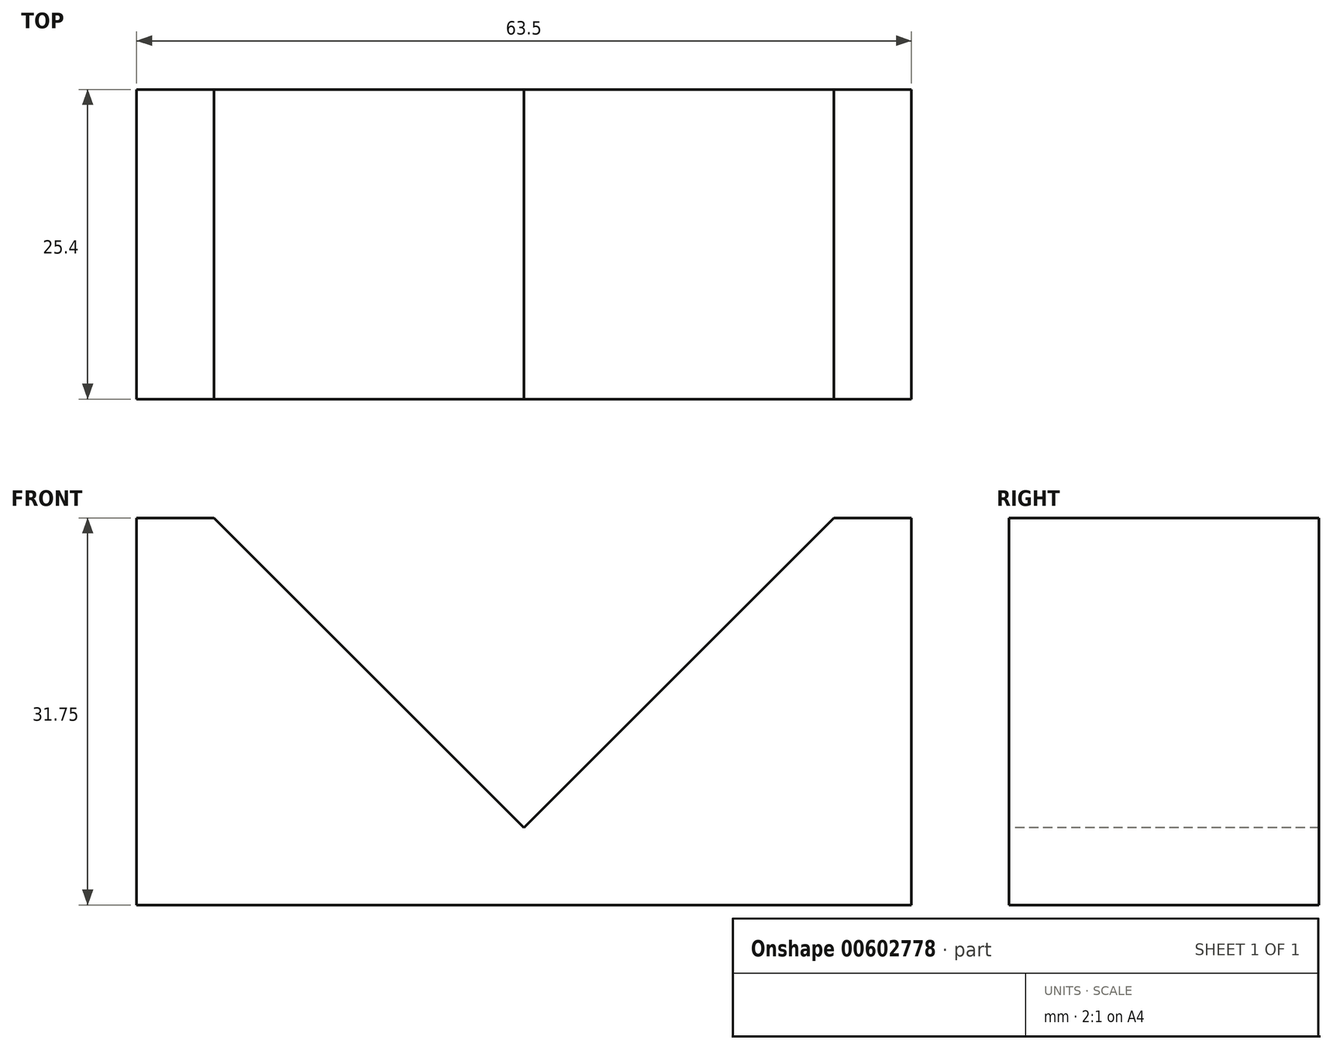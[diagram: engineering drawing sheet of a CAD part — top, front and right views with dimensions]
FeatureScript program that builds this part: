
annotation { "Feature Type Name" : "Feature", "Feature Type Description" : "" }
export const myFeature = defineFeature(function(context is Context, id is Id, definition is map)
    precondition{}
    {
        {
            var Q0;
            Q0=qCreatedBy(makeId("Front.planeOp"),FACE);
            var sketch = newSketch(context, id + "F0", { "sketchPlane" : qUnion([Q0])});
            skLineSegment(sketch, "E0", {"start": v(0, 0) * mm, "end": v(63.5, 0) * mm});
            skLineSegment(sketch, "E1", {"start": v(63.5, 0) * mm, "end": v(63.5, 31.75) * mm});
            skLineSegment(sketch, "E2", {"start": v(63.5, 31.75) * mm, "end": v(0, 31.75) * mm});
            skLineSegment(sketch, "E3", {"start": v(0, 31.75) * mm, "end": v(0, 0) * mm});
            skSolve(sketch);
        }
        {
            var Q0;
            Q0=makeQuery(id+"F0.imprint","IMPRINT",FACE,{"disambiguationData":[TD([[makeQuery(id+"F0.imprint","IMPRINT",EDGE,{"derivedFrom":sQuery(id+"F0.wireOp",EDGE,"E0")}),1.0]])]});
            extrude(context, id + "F1", {"entities" : qUnion([Q0]), "depth" : 25.4 * mm, "offsetDistance" : 25.4 * mm});
        }
        {
            var Q0;
            Q0=makeQuery(id+"F1.opExtrude","CAP_FACE",FACE,{"disambiguationData":[OSD([sQuery(id+"F0.wireOp",EDGE,"E0"),sQuery(id+"F0.wireOp",EDGE,"E1"),sQuery(id+"F0.wireOp",EDGE,"E2"),sQuery(id+"F0.wireOp",EDGE,"E3")])],"isStart":false});
            var sketch = newSketch(context, id + "F2", { "sketchPlane" : qUnion([Q0])});
            skLineSegment(sketch, "E4", {"start": v(0, 31.75) * mm, "end": v(6.35, 31.75) * mm});
            skLineSegment(sketch, "E5", {"start": v(63.5, 31.75) * mm, "end": v(57.15, 31.75) * mm});
            skLineSegment(sketch, "E6", {"start": v(0, 0) * mm, "end": v(31.75, 0) * mm});
            skLineSegment(sketch, "E7", {"start": v(31.75, 0) * mm, "end": v(31.75, 6.35) * mm});
            skLineSegment(sketch, "E8", {"start": v(31.75, 6.35) * mm, "end": v(6.35, 31.75) * mm});
            skLineSegment(sketch, "E9", {"start": v(31.75, 6.35) * mm, "end": v(57.15, 31.75) * mm});
            skLineSegment(sketch, "E10", {"start": v(0, 31.75) * mm, "end": v(19.05, 31.75) * mm});
            skLineSegment(sketch, "E11", {"start": v(19.05, 31.75) * mm, "end": v(63.5, 31.75) * mm});
            skLineSegment(sketch, "E12", {"start": v(44.45, 31.75) * mm, "end": v(63.5, 31.75) * mm});
            skLineSegment(sketch, "E13", {"start": v(31.75, 0) * mm, "end": v(31.75, 19.05) * mm});
            skLineSegment(sketch, "E14", {"start": v(44.45, 31.75) * mm, "end": v(31.75, 19.05) * mm});
            skLineSegment(sketch, "E15", {"start": v(19.05, 31.75) * mm, "end": v(31.75, 19.05) * mm});
            skSolve(sketch);
        }
        {
            var Q0;
            Q0=makeQuery(id+"F2.imprint","IMPRINT",FACE,{"disambiguationData":[TD([[makeQuery(id+"F2.imprint","IMPRINT",EDGE,{"derivedFrom":sQuery(id+"F2.wireOp",EDGE,"E11")}),1.0]])]});
            var Q1;
            {var subQ0=sQuery(id+"F2.wireOp",EDGE,"E8");Q1=makeQuery(id+"F2.imprint","IMPRINT",FACE,{"disambiguationData":[TD([[makeQuery(id+"F2.imprint","IMPRINT",EDGE,{"derivedFrom":subQ0}),-1.0]])]});}
            var Q2;
            {var subQ0=sQuery(id+"F2.wireOp",EDGE,"E9");Q2=makeQuery(id+"F2.imprint","IMPRINT",FACE,{"disambiguationData":[TD([[makeQuery(id+"F2.imprint","IMPRINT",EDGE,{"derivedFrom":subQ0}),1.0]])]});}
            extrude(context, id + "F3", {"entities" : qUnion([Q0, Q1, Q2]), "operationType" : NewBodyOperationType.REMOVE, "oppositeDirection" : true, "depth" : 25.4 * mm, "offsetDistance" : 25.4 * mm});
        }
    });
